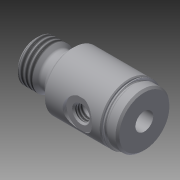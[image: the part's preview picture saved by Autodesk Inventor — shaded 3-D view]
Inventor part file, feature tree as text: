
AUTODESK INVENTOR PART (.ipt)
format: ipt  version: 2014 SP2 (Build 180246200, 246)  size: 261,632 bytes
history: native  units: in
note: dims shown in document units (in); Inventor stores cm internally (conversion verified against a paired STEP export)
features: other x119, sketch x5, revolve x4, thread x2, hole x1
ambient origin geometry x8: Origin, YZ Plane, XZ Plane, XY Plane, X Axis, Y Axis, Z Axis, Center Point
bodies: Solid1 (feature_tree)
feature tree (131):
  revolve  "Revolution1"  [1 undecoded]
  thread  "Thread1"  [1 undecoded]
  revolve  "Revolution2"  Angle=360.0deg
  hole  "Hole1"  [1 undecoded]
  revolve  "Revolution3"  [1 undecoded]
  thread  "Thread2"  [1 undecoded]
  revolve  "Revolution4"  [1 undecoded]
  other  "dp1_XY"
  other  "dp1_YZ"
  other  "dp1_ZX"
  other  "dp1_X"
  other  "dp1_Y"
  other  "dp1_Z"
  other  "dp1_Center"
  other  "dp2_XY"
  other  "dp2_YZ"
  other  "dp2_ZX"
  other  "dp2_X"
  other  "dp2_Y"
  other  "dp2_Z"
  other  "dp2_Center"
  other  "hh_XY"
  other  "hh_YZ"
  other  "hh_ZX"
  other  "hh_X"
  other  "hh_Y"
  other  "hh_Z"
  other  "hh_Center"
  other  "port_XY"
  other  "port_YZ"
  other  "port_ZX"
  other  "port_X"
  other  "port_Y"
  other  "port_Z"
  other  "port_Center"
  other  "rod_guide_XY"
  other  "rod_guide_YZ"
  other  "rod_guide_ZX"
  other  "rod_guide_X"
  other  "rod_guide_Y"
  other  "rod_guide_Z"
  other  "rod_guide_Center"
  other  "s1_XY"
  other  "s1_YZ"
  other  "s1_ZX"
  other  "s1_X"
  other  "s1_Y"
  other  "s1_Z"
  other  "s1_Center"
  other  "s2_XY"
  other  "s2_YZ"
  other  "s2_ZX"
  other  "s2_X"
  other  "s2_Y"
  other  "s2_Z"
  other  "s2_Center"
  other  "t1_XY"
  other  "t1_YZ"
  other  "t1_ZX"
  other  "t1_X"
  other  "t1_Y"
  other  "t1_Z"
  other  "t1_Center"
  other  "t111_XY"
  other  "t111_YZ"
  other  "t111_ZX"
  other  "t111_X"
  other  "t111_Y"
  other  "t111_Z"
  other  "t111_Center"
  other  "to_foot_bracket_XY"
  other  "to_foot_bracket_YZ"
  other  "to_foot_bracket_ZX"
  other  "to_foot_bracket_X"
  other  "to_foot_bracket_Y"
  other  "to_foot_bracket_Z"
  other  "to_foot_bracket_Center"
  other  "to_nut_XY"
  other  "to_nut_YZ"
  other  "to_nut_ZX"
  other  "to_nut_X"
  other  "to_nut_Y"
  other  "to_nut_Z"
  other  "to_nut_Center"
  other  "to_rod_XY"
  other  "to_rod_YZ"
  other  "to_rod_ZX"
  other  "to_rod_X"
  other  "to_rod_Y"
  other  "to_rod_Z"
  other  "to_rod_Center"
  other  "to_screw_XY"
  other  "to_screw_YZ"
  other  "to_screw_ZX"
  other  "to_screw_X"
  other  "to_screw_Y"
  other  "to_screw_Z"
  other  "to_screw_Center"
  other  "to_trunnion_brackets_XY"
  other  "to_trunnion_brackets_YZ"
  other  "to_trunnion_brackets_ZX"
  other  "to_trunnion_brackets_X"
  other  "to_trunnion_brackets_Y"
  other  "to_trunnion_brackets_Z"
  other  "to_trunnion_brackets_Center"
  other  "to_trunnion_brackets1_XY"
  other  "to_trunnion_brackets1_YZ"
  other  "to_trunnion_brackets1_ZX"
  other  "to_trunnion_brackets1_X"
  other  "to_trunnion_brackets1_Y"
  other  "to_trunnion_brackets1_Z"
  other  "to_trunnion_brackets1_Center"
  other  "to_trunnion_brackets2_XY"
  other  "to_trunnion_brackets2_YZ"
  other  "to_trunnion_brackets2_ZX"
  other  "to_trunnion_brackets2_X"
  other  "to_trunnion_brackets2_Y"
  other  "to_trunnion_brackets2_Z"
  other  "to_trunnion_brackets2_Center"
  other  "to_tube_XY"
  other  "to_tube_YZ"
  other  "to_tube_ZX"
  other  "to_tube_X"
  other  "to_tube_Y"
  other  "to_tube_Z"
  other  "to_tube_Center"
  sketch  "Sketch_2"  dims[d0=360.0deg d1=0.1537in d2=0.0in d3=360.0deg]
  sketch  "Sketch_3"  dims[d4=0.19in d5=0.75in d6=0.23in d7=0.25in d8=90.0deg d9=1.156in d10=0.0in d11=360.0deg]
  sketch  "Sketch3"  dims[d12=0.0786in d13=0.0in d14=360.0deg]
  sketch  "Sketch_12"  dims[d15=0.0in d16=0.0in d17=0.0in d18=0.0in d19=0.0in d20=0.0in]
  sketch  "Sketch_47"
note: 6 required parameter values undecoded (feature->parameter linkage not recoverable at this tier; creation-order binding heuristic only, values carry confidence <= 0.55)